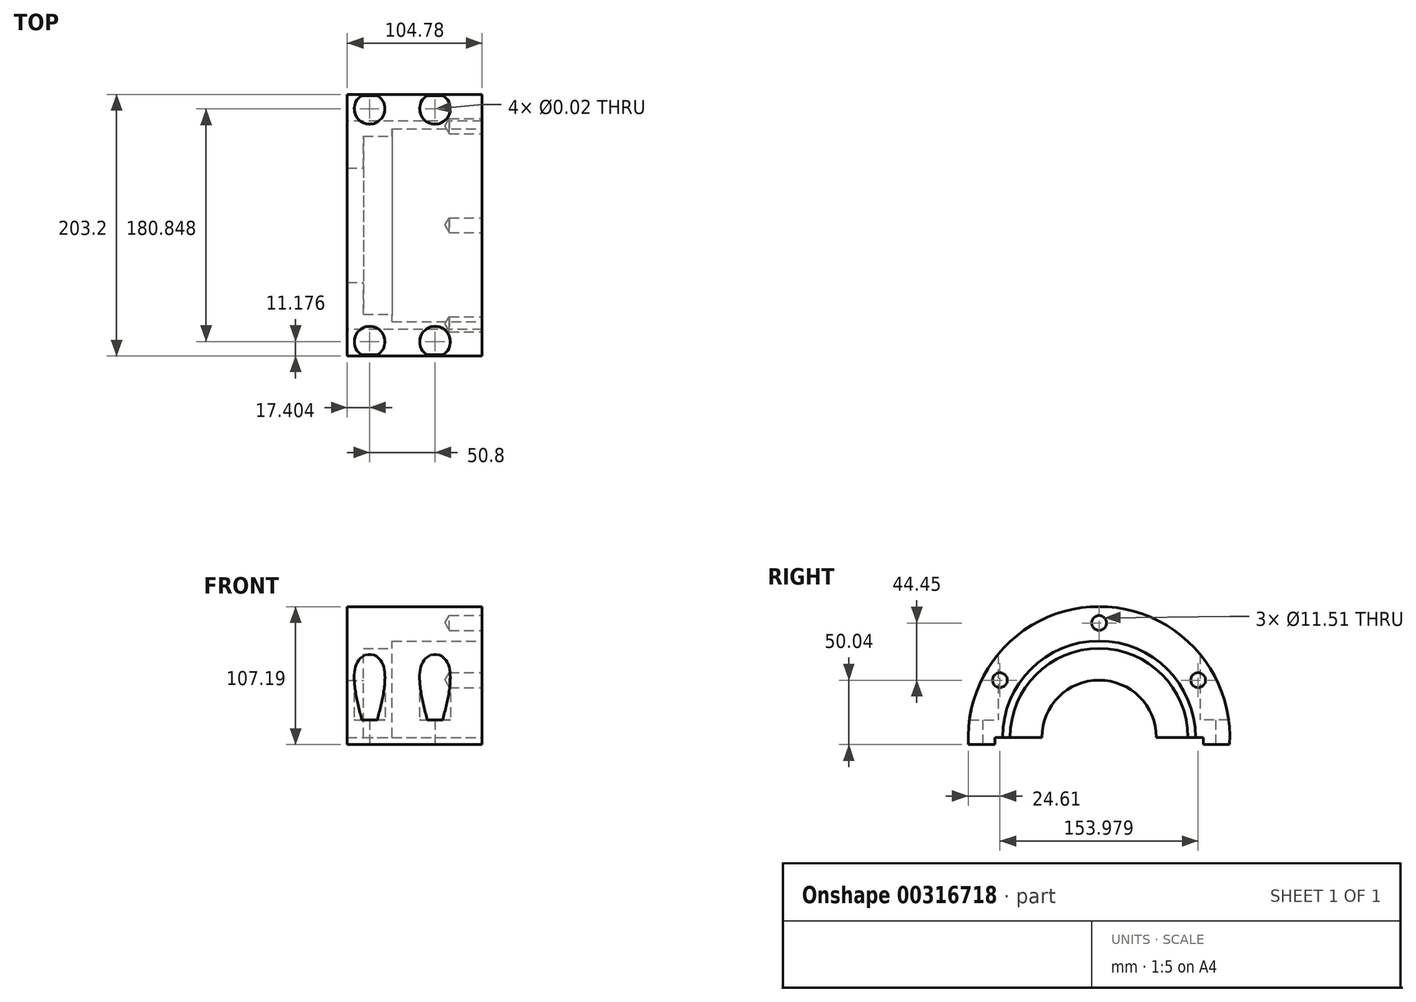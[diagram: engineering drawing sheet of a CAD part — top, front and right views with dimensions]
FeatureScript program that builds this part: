
annotation { "Feature Type Name" : "Feature", "Feature Type Description" : "" }
export const myFeature = defineFeature(function(context is Context, id is Id, definition is map)
    precondition{}
    {
        {
            var Q0;
            Q0=qCreatedBy(makeId("Right.planeOp"),FACE);
            var sketch = newSketch(context, id + "F0", { "sketchPlane" : qUnion([Q0])});
            skCircle(sketch, "E0", {"center": v(0, 0) * mm, "radius": 101.6 * mm});
            skSolve(sketch);
        }
        {
            var Q0;
            Q0 = qSketchRegion(id + "F0", true);
            extrude(context, id + "F1", {"entities" : qUnion([Q0]), "oppositeDirection" : true, "depth" : 104.77 * mm});
        }
        {
            var Q0;
            Q0=makeQuery(id+"F1.opExtrude","CAP_FACE",FACE,{"disambiguationData":[OSD([sQuery(id+"F0.wireOp",EDGE,"E0")])],"isStart":true});
            var sketch = newSketch(context, id + "F2", { "sketchPlane" : qUnion([Q0])});
            skPoint(sketch, "E1", {"position": v(0, 0) * mm});
            skSolve(sketch);
        }
        {
            var Q0;
            Q0=sQuery(id+"F2.wireOp",VERTEX,"E1");
            var Q1;
            Q1=makeQuery(id+"F1.opExtrude","SWEPT_BODY",BODY,{"disambiguationData":[OSD([sQuery(id+"F0.wireOp",EDGE,"E0")])]});
            hole(context, id + "F3", {"style" : HoleStyle.C_BORE, "endStyle" : HoleEndStyle.THROUGH, "holeDiameter" : 88.9 * mm, "cBoreDiameter" : 138.18 * mm, "cBoreDepth" : 92.07 * mm, "tappedDepth" : 25.9 * mm, "tapClearance" : 3, "locations" : qUnion([Q0]), "scope" : qUnion([Q1])});
        }
        {
            var Q0;
            Q0=makeQuery(id+"F1.opExtrude","CAP_FACE",FACE,{"disambiguationData":[OSD([sQuery(id+"F0.wireOp",EDGE,"E0")])],"isStart":true});
            var sketch = newSketch(context, id + "F4", { "sketchPlane" : qUnion([Q0])});
            skCircle(sketch, "E2", {"center": v(0, 0) * mm, "radius": 74.93 * mm});
            skSolve(sketch);
        }
        {
            var Q0;
            Q0 = qSketchRegion(id + "F4", true);
            extrude(context, id + "F5", {"entities" : qUnion([Q0]), "operationType" : NewBodyOperationType.REMOVE, "oppositeDirection" : true, "depth" : 69.85 * mm});
        }
        {
            var Q0;
            Q0=makeQuery(id+"F1.opExtrude","CAP_FACE",FACE,{"disambiguationData":[OSD([sQuery(id+"F0.wireOp",EDGE,"E0")])],"isStart":true});
            var sketch = newSketch(context, id + "F6", { "sketchPlane" : qUnion([Q0])});
            skLineSegment(sketch, "E3", {"start": v(-134.97, 0) * mm, "end": v(144.4, 0) * mm, "construction": true});
            skLineSegment(sketch, "E4.0", {"start": v(-134.97, -5.59) * mm, "end": v(144.4, -5.59) * mm, "construction": true});
            skLineSegment(sketch, "E5.bottom", {"start": v(-134.97, -5.59) * mm, "end": v(153.54, -5.59) * mm});
            skLineSegment(sketch, "E5.top", {"start": v(-134.97, -103.44) * mm, "end": v(153.54, -103.44) * mm});
            skLineSegment(sketch, "E5.left", {"start": v(-134.97, -5.59) * mm, "end": v(-134.97, -103.44) * mm});
            skLineSegment(sketch, "E5.right", {"start": v(153.54, -5.59) * mm, "end": v(153.54, -103.44) * mm});
            skSolve(sketch);
        }
        {
            var Q0;
            Q0 = qSketchRegion(id + "F6", true);
            extrude(context, id + "F7", {"entities" : qUnion([Q0]), "operationType" : NewBodyOperationType.REMOVE, "endBound" : BoundingType.THROUGH_ALL, "oppositeDirection" : true, "depth" : 25.4 * mm});
        }
        {
            var Q0;
            Q0=makeQuery(id+"F1.opExtrude","CAP_FACE",FACE,{"disambiguationData":[OSD([sQuery(id+"F0.wireOp",EDGE,"E0")])],"isStart":true});
            var sketch = newSketch(context, id + "F8", { "sketchPlane" : qUnion([Q0])});
            skLineSegment(sketch, "E6", {"start": v(-144.4, 0) * mm, "end": v(151.77, 0) * mm, "construction": true});
            skLineSegment(sketch, "E7", {"start": v(0, 119.91) * mm, "end": v(0, -39.22) * mm, "construction": true});
            skLineSegment(sketch, "E8.0", {"start": v(-80.96, 119.91) * mm, "end": v(-80.96, -39.22) * mm, "construction": true});
            skLineSegment(sketch, "E9.bottom", {"start": v(-80.96, 0) * mm, "end": v(0, 0) * mm});
            skLineSegment(sketch, "E9.top", {"start": v(-80.96, -28.03) * mm, "end": v(0, -28.03) * mm});
            skLineSegment(sketch, "E9.left", {"start": v(-80.96, 0) * mm, "end": v(-80.96, -28.03) * mm});
            skLineSegment(sketch, "E9.right", {"start": v(0, 0) * mm, "end": v(0, -28.03) * mm});
            skLineSegment(sketch, "E10.MirrorCS", {"start": v(80.96, 0) * mm, "end": v(80.96, -28.03) * mm});
            skLineSegment(sketch, "E11.MirrorCS", {"start": v(80.96, -28.03) * mm, "end": v(0, -28.03) * mm});
            skLineSegment(sketch, "E12.MirrorCS", {"start": v(80.96, 0) * mm, "end": v(0, 0) * mm});
            skSolve(sketch);
        }
        {
            var Q0;
            Q0 = qSketchRegion(id + "F8", true);
            extrude(context, id + "F9", {"entities" : qUnion([Q0]), "operationType" : NewBodyOperationType.REMOVE, "endBound" : BoundingType.THROUGH_ALL, "oppositeDirection" : true, "depth" : 25.4 * mm});
        }
        {
            var Q0;
            Q0=makeQuery(id+"F7.boolean.opBoolean","COPY",FACE,{"disambiguationData":[OD(0.0)],"derivedFrom":makeQuery(id+"F7.opExtrude","SWEPT_FACE",FACE,{"disambiguationData":[OSD([sQuery(id+"F6.wireOp",EDGE,"E5.bottom")])]})});
            var sketch = newSketch(context, id + "F10", { "sketchPlane" : qUnion([Q0])});
            skLineSegment(sketch, "E13", {"start": v(48.99, 0) * mm, "end": v(-129.6, 0) * mm, "construction": true});
            skLineSegment(sketch, "E14.0", {"start": v(0, 101.45) * mm, "end": v(0, 80.96) * mm, "construction": true});
            skLineSegment(sketch, "E15.0", {"start": v(48.99, 90.42) * mm, "end": v(-129.6, 90.42) * mm, "construction": true});
            skLineSegment(sketch, "E16.0", {"start": v(-36.58, 101.45) * mm, "end": v(-36.58, 80.96) * mm, "construction": true});
            skLineSegment(sketch, "E17.0", {"start": v(-87.38, 101.45) * mm, "end": v(-87.38, 80.96) * mm, "construction": true});
            skPoint(sketch, "E18", {"position": v(-36.58, 90.42) * mm});
            skPoint(sketch, "E19", {"position": v(-87.38, 90.42) * mm});
            skPoint(sketch, "E20.MirrorP", {"position": v(-36.58, -90.42) * mm});
            skPoint(sketch, "E21.MirrorP", {"position": v(-87.38, -90.42) * mm});
            skSolve(sketch);
        }
        {
            var Q0;
            Q0=sQuery(id+"F10.wireOp",VERTEX,"E18");
            var Q1;
            Q1=sQuery(id+"F10.wireOp",VERTEX,"E19");
            var Q2;
            Q2=sQuery(id+"F10.wireOp",VERTEX,"E20.MirrorP");
            var Q3;
            Q3=sQuery(id+"F10.wireOp",VERTEX,"E21.MirrorP");
            var Q4;
            Q4=makeQuery(id+"F1.opExtrude","SWEPT_BODY",BODY,{"disambiguationData":[OSD([sQuery(id+"F0.wireOp",EDGE,"E0")])]});
            hole(context, id + "F11", {"style" : HoleStyle.SIMPLE, "endStyle" : HoleEndStyle.THROUGH, "standardTappedOrClearance" : lookupTablePath({ "standard" : "ANSI", "size" : "9/16 (0.56)", "type" : "Drilled" }), "standardBlindInLast" : lookupTablePath({ "standard" : "ANSI", "size" : "9/16", "type" : "Drilled" }), "holeDiameter" : 9 / 406.4 * mm, "tappedDepth" : 25.88 * mm, "tapClearance" : 3, "locations" : qUnion([Q0, Q1, Q2, Q3]), "scope" : qUnion([Q4])});
        }
        {
            var Q0;
            Q0=makeQuery(id+"F7.boolean.opBoolean","COPY",FACE,{"disambiguationData":[OD(0.0)],"derivedFrom":makeQuery(id+"F7.opExtrude","SWEPT_FACE",FACE,{"disambiguationData":[OSD([sQuery(id+"F6.wireOp",EDGE,"E5.bottom")])]})});
            cPlane(context, id + "F12", {"entities" : qUnion([Q0]), "cplaneType" : CPlaneType.OFFSET, "offset" : 19.05 * mm, "oppositeDirection" : true, "width" : 152.4 * mm, "height" : 152.4 * mm});
        }
        {
            var Q0;
            Q0=qCreatedBy(id+"F12.planeOp",FACE);
            var sketch = newSketch(context, id + "F13", { "sketchPlane" : qUnion([Q0])});
            skCircle(sketch, "E22.0", {"center": v(-87.38, 90.42) * mm, "radius": 7.14 * mm, "construction": true});
            skCircle(sketch, "E23.0", {"center": v(-36.58, 90.42) * mm, "radius": 7.14 * mm, "construction": true});
            skCircle(sketch, "E24.0", {"center": v(-87.38, -90.42) * mm, "radius": 7.14 * mm, "construction": true});
            skCircle(sketch, "E25.0", {"center": v(-36.58, -90.42) * mm, "radius": 7.14 * mm, "construction": true});
            skLineSegment(sketch, "E26.0", {"start": v(-104.78, 101.6) * mm, "end": v(-104.78, -101.6) * mm, "construction": true});
            skLineSegment(sketch, "E27", {"start": v(101.37, 0) * mm, "end": v(-145.5, 0) * mm, "construction": true});
            skCircle(sketch, "E28", {"center": v(-87.38, 90.42) * mm, "radius": 11.94 * mm});
            skCircle(sketch, "E29", {"center": v(-36.58, 90.42) * mm, "radius": 11.94 * mm});
            skCircle(sketch, "E30.MirrorC", {"center": v(-87.38, -90.42) * mm, "radius": 11.94 * mm});
            skCircle(sketch, "E31.MirrorC", {"center": v(-36.58, -90.42) * mm, "radius": 11.94 * mm});
            skSolve(sketch);
        }
        {
            var Q0;
            Q0 = qSketchRegion(id + "F13", true);
            extrude(context, id + "F14", {"entities" : qUnion([Q0]), "operationType" : NewBodyOperationType.REMOVE, "endBound" : BoundingType.THROUGH_ALL, "oppositeDirection" : true, "depth" : 25.4 * mm});
        }
        {
            var Q0;
            Q0=makeQuery(id+"F1.opExtrude","CAP_FACE",FACE,{"disambiguationData":[OSD([sQuery(id+"F0.wireOp",EDGE,"E0")])],"isStart":true});
            var sketch = newSketch(context, id + "F15", { "sketchPlane" : qUnion([Q0])});
            skLineSegment(sketch, "E32", {"start": v(0, 0) * mm, "end": v(0, 141.98) * mm, "construction": true});
            skLineSegment(sketch, "E33", {"start": v(0, 0) * mm, "end": v(-175.98, 101.6) * mm, "construction": true});
            skPoint(sketch, "E33.endSnap0", {"position": v(0, 101.6) * mm});
            skCircle(sketch, "E34", {"center": v(0, 0) * mm, "radius": 88.9 * mm, "construction": true});
            skPoint(sketch, "E35", {"position": v(-76.99, 44.45) * mm});
            skPoint(sketch, "E36", {"position": v(0, 88.9) * mm});
            skPoint(sketch, "E37.MirrorP", {"position": v(76.99, 44.45) * mm});
            skSolve(sketch);
        }
        {
            var Q0;
            Q0=sQuery(id+"F15.wireOp",VERTEX,"E35");
            var Q1;
            Q1=sQuery(id+"F15.wireOp",VERTEX,"E36");
            var Q2;
            Q2=sQuery(id+"F15.wireOp",VERTEX,"E37.MirrorP");
            var Q3;
            Q3=makeQuery(id+"F1.opExtrude","SWEPT_BODY",BODY,{"disambiguationData":[OSD([sQuery(id+"F0.wireOp",EDGE,"E0")])]});
            hole(context, id + "F16", {"style" : HoleStyle.SIMPLE, "endStyle" : HoleEndStyle.BLIND, "standardTappedOrClearance" : lookupTablePath({ "standard" : "ANSI", "engagement" : "75%", "pitch" : "20 tpi", "size" : "1/2", "type" : "Tapped" }), "standardBlindInLast" : lookupTablePath({ "standard" : "ANSI", "engagement" : "75%", "pitch" : "20 tpi", "size" : "1/2", "type" : "Tapped" }), "holeDiameter" : 11.5 * mm, "showTappedDepth" : true, "holeDepth" : 25.4 * mm, "tappedDepth" : 21.59 * mm, "tapClearance" : 3, "locations" : qUnion([Q0, Q1, Q2]), "scope" : qUnion([Q3]), "majorDiameter" : 12.7 * mm});
        }
    });
